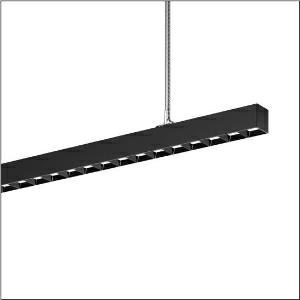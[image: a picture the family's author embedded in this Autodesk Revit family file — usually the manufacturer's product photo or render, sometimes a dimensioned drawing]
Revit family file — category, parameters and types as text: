
# Revit family: silica_r__21_51mx32dc3dbb_53cb
name_source: partatom
category: Lighting Fixtures
units: mm (PartAtom-declared; Revit-internal decimal feet)

## family parameters
Cut with Voids When Loaded = No
Host = Face
Light Source = No
Part Type = Normal
Room Calculation Point = No
Round Connector Dimension = Use Diameter
Shared = No

## types (1)
- --- (1 x LED, 18220 lm, 113 W, 3000K)
    Apparent Load = 113 VA
    CIE Flux Codes = 86 99 100 59 100
    Color Rendering = 80
    Color Temperature = 3000K
    Default Elevation = 1800 mm
    Description = Silica® 21, office luminaire, primary light control with darklight reflector, of PMMA, black, CAT 2 (L<= 3000cd/m²), light emission: direct/indirect distribution, primary light characteristic: symmetric, installation type: suspended mounting, LED, rated luminous flux: 18.220lm, luminous efficacy: 161lm/W, light colour: 830, colour temperature: 3000K, with terminal, 3+2-pole, max. 2.5mm², mains connection: 220..240V, AC, 50/60Hz, rated input power: 113W, luminaire housing, of aluminium, jet black (RAL 9005), length: 3.004mm, width: 53mm, height: 53mm, protection rating (complete): IP20, insulation class (complete): insulation class I (protective earthing), certification: CE, permissible operating ambient temperature: 0..+35°C, standard: EN 50419, packaging unit: 1 piece
    Height = 53 mm
    Lamp = 1 x LED
    Lamp Light Flux = 18220 lm
    Lamp Power = 113 W
    Lamp count = 1
    Length = 3004 mm
    Luminous efficacy = 161 lm/W
    Manufacturer = Siteco
    ModVariant = No
    Model = 51MX32DC3DBB
    Mounting Place = Ceiling
    Mounting Type = Pendant
    Number of Poles = 1
    OnlyDefault = Yes
    Power Factor = 1
    Product Name = Silica® 21
    Product group = office luminaire | ceiling pendant
    ProductGroupID = 902
    Protection Class = Protection class I
    Protection Degree = IP 20
    RLX_Detail_Level = 1
    RLX_Emergency_Light_Flux = 0 lm
    RLX_Emergency_Type = 0
    RLX_Emergency_Type_DB = No
    RlxData = <blob elided: 66281 chars, md5=1b1d7a72>
    Socket = socket
    Standby Power = 0 W
    System Light Flux = 18220 lm
    System Power = 113 W
    Type Comments = factory setting: luminous flux: 100 % | dim-lin: 254 | 391 mA
    Type Image = l_1297774.jpg
    URL = http://relux.com
    VarID = @adj_052763
    Voltage = 0 V
    Weight = 0.00 kg
    Width = 53 mm

## geometry (parser evidence)
native form markers: Blend x4, Sweep x12
no freeform markers — native parametric forms only
